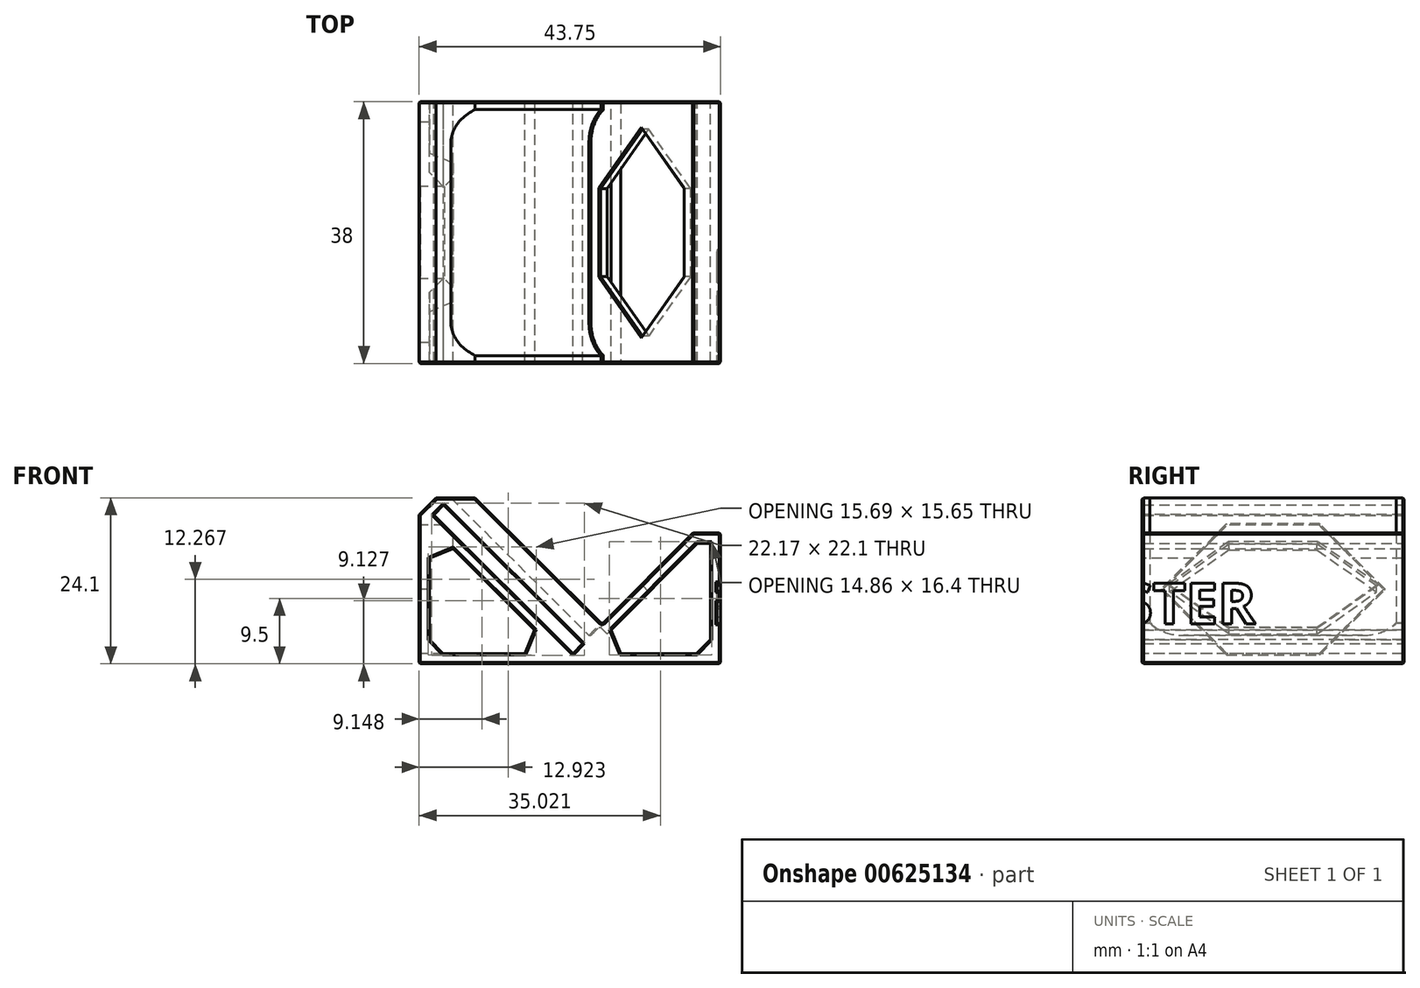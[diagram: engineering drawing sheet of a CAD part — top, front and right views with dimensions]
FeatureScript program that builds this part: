
annotation { "Feature Type Name" : "Feature", "Feature Type Description" : "" }
export const myFeature = defineFeature(function(context is Context, id is Id, definition is map)
    precondition{}
    {
        {
            var Q0;
            Q0=qCreatedBy(makeId("Front.planeOp"),FACE);
            var sketch = newSketch(context, id + "F0", { "sketchPlane" : qUnion([Q0])});
            skLineSegment(sketch, "E0", {"start": v(0, 0) * mm, "end": v(0, 19) * mm});
            skLineSegment(sketch, "E1", {"start": v(-4, 19) * mm, "end": v(-18.97, 3.98) * mm});
            skLineSegment(sketch, "E2", {"start": v(-18.97, 3.98) * mm, "end": v(-40.22, 25.16) * mm});
            skLineSegment(sketch, "E3", {"start": v(-23.56, 1.5) * mm, "end": v(-42.25, 20.12) * mm});
            skPoint(sketch, "E4", {"position": v(0, 0) * mm});
            skLineSegment(sketch, "E5", {"start": v(-40.21, 23.03) * mm, "end": v(-20.03, 2.92) * mm});
            skLineSegment(sketch, "E6", {"start": v(-20.03, 2.92) * mm, "end": v(-21.44, 1.5) * mm});
            skLineSegment(sketch, "E7", {"start": v(0, 19) * mm, "end": v(-4, 19) * mm});
            skLineSegment(sketch, "E8", {"start": v(-19.32, 1.5) * mm, "end": v(-3.38, 17.5) * mm});
            skLineSegment(sketch, "E9", {"start": v(-3.38, 17.5) * mm, "end": v(-1.5, 17.5) * mm});
            skLineSegment(sketch, "E10", {"start": v(-1.5, 17.5) * mm, "end": v(-1.5, 1.5) * mm});
            skLineSegment(sketch, "E11", {"start": v(-1.5, 1.5) * mm, "end": v(-19.32, 1.5) * mm});
            skLineSegment(sketch, "E12", {"start": v(-21.44, 1.5) * mm, "end": v(-41.63, 21.62) * mm});
            skLineSegment(sketch, "E13", {"start": v(-40.21, 23.03) * mm, "end": v(-41.63, 21.62) * mm});
            skLineSegment(sketch, "E14", {"start": v(-40.22, 25.16) * mm, "end": v(-43.75, 21.61) * mm});
            skLineSegment(sketch, "E15", {"start": v(-43.75, 21.61) * mm, "end": v(-43.75, 0) * mm});
            skLineSegment(sketch, "E16", {"start": v(-43.75, 0) * mm, "end": v(0, 0) * mm});
            skLineSegment(sketch, "E17.0", {"start": v(-42.25, 1.5) * mm, "end": v(-23.56, 1.5) * mm});
            skLineSegment(sketch, "E17.1", {"start": v(-42.25, 20.12) * mm, "end": v(-42.25, 1.5) * mm});
            skSolve(sketch);
        }
        {
            var Q0;
            {var subQ3=sQuery(id+"F0.wireOp",EDGE,"E2");Q0=makeQuery(id+"F0.imprint","IMPRINT",FACE,{"disambiguationData":[TD([[makeQuery(id+"F0.imprint","IMPRINT",EDGE,{"derivedFrom":subQ3}),1.0]])]});}
            extrude(context, id + "F1", {"entities" : qUnion([Q0]), "endBound" : BoundingType.SYMMETRIC, "depth" : 38 * mm, "offsetDistance" : 25 * mm});
        }
        {
            var Q0;
            Q0=makeQuery(id+"F1.opExtrude","SWEPT_FACE",FACE,{"disambiguationData":[OSD([sQuery(id+"F0.wireOp",EDGE,"E0")])]});
            var sketch = newSketch(context, id + "F2", { "sketchPlane" : qUnion([Q0])});
            skText(sketch, "E18", { "text": "AIRSTER", "fontName": "OpenSans-Bold.ttf"});
            skPoint(sketch, "E19", {"position": v(-17, 9.5) * mm});
            skPoint(sketch, "E20", {"position": v(-19, 9.5) * mm});
            skPoint(sketch, "E21", {"position": v(0, 19) * mm});
            const initialGuessF2  = {"E18": [-0.036, 0.00576, 1, 0, 0.00598]};
            skSetInitialGuess(sketch, initialGuessF2);
            skSolve(sketch);
        }
        {
            var Q0;
            Q0=qSketchRegion(id+"F2",true);
            extrude(context, id + "F3", {"entities" : qUnion([Q0]), "operationType" : NewBodyOperationType.REMOVE, "oppositeDirection" : true, "depth" : 0.5 * mm});
        }
        {
            var Q0;
            Q0=makeQuery(id+"F1.opExtrude","SWEPT_EDGE",EDGE,{"disambiguationData":[OSD([sQuery(id+"F0.wireOp",EDGE,"E8"),sQuery(id+"F0.wireOp",EDGE,"E11")])]});
            var Q1;
            Q1=makeQuery(id+"F1.opExtrude","SWEPT_EDGE",EDGE,{"disambiguationData":[OSD([sQuery(id+"F0.wireOp",EDGE,"E10"),sQuery(id+"F0.wireOp",EDGE,"E11")])]});
            var Q2;
            Q2=makeQuery(id+"F1.opExtrude","SWEPT_EDGE",EDGE,{"disambiguationData":[OSD([sQuery(id+"F0.wireOp",EDGE,"E17.0"),sQuery(id+"F0.wireOp",EDGE,"E17.1")])]});
            var Q3;
            Q3=makeQuery(id+"F1.opExtrude","SWEPT_EDGE",EDGE,{"disambiguationData":[OSD([sQuery(id+"F0.wireOp",EDGE,"E3"),sQuery(id+"F0.wireOp",EDGE,"E17.1")])]});
            chamfer(context, id + "F4", {"entities" : qUnion([Q0, Q1, Q2, Q3]), "width" : 2 * mm, "tangentPropagation" : true});
        }
        {
            var Q0;
            Q0=makeQuery(id+"F1.opExtrude","SWEPT_FACE",FACE,{"disambiguationData":[OSD([sQuery(id+"F0.wireOp",EDGE,"E1")])]});
            var sketch = newSketch(context, id + "F5", { "sketchPlane" : qUnion([Q0])});
            skArc(sketch, "E22", {"start": v(-19, -4.57) * mm, "mid": v(-17.24, -8.81) * mm, "end": v(-13, -10.57) * mm});
            skArc(sketch, "E23.MirrorCS", {"start": v(19, -4.57) * mm, "mid": v(17.24, -8.81) * mm, "end": v(13, -10.57) * mm});
            skLineSegment(sketch, "E24", {"start": v(-19, -8.07) * mm, "end": v(-17.87, -8.07) * mm});
            skLineSegment(sketch, "E25.MirrorCS", {"start": v(19, -8.07) * mm, "end": v(17.87, -8.07) * mm});
            skLineSegment(sketch, "E26", {"start": v(0, 8.63) * mm, "end": v(-15, 8.63) * mm});
            skLineSegment(sketch, "E27", {"start": v(-15, 8.63) * mm, "end": v(-15, -8.57) * mm});
            skLineSegment(sketch, "E28", {"start": v(-15, -8.57) * mm, "end": v(0, -8.57) * mm});
            skLineSegment(sketch, "E29.MirrorCS", {"start": v(0, 8.63) * mm, "end": v(15, 8.63) * mm});
            skLineSegment(sketch, "E30.MirrorCS", {"start": v(15, 8.63) * mm, "end": v(15, -8.57) * mm});
            skLineSegment(sketch, "E31.MirrorCS", {"start": v(15, -8.57) * mm, "end": v(0, -8.57) * mm});
            skPoint(sketch, "E32", {"position": v(-15, 0.03) * mm});
            skLineSegment(sketch, "E33", {"start": v(-15, 0.03) * mm, "end": v(-6.4, 8.63) * mm});
            skLineSegment(sketch, "E34", {"start": v(-15, 0.03) * mm, "end": v(-6.4, -8.57) * mm});
            skLineSegment(sketch, "E35.MirrorCS", {"start": v(15, 0.03) * mm, "end": v(6.4, 8.63) * mm});
            skLineSegment(sketch, "E36.MirrorCS", {"start": v(15, 0.03) * mm, "end": v(6.4, -8.57) * mm});
            skSolve(sketch);
        }
        {
            var Q0;
            {var subQ4=sQuery(id+"F5.wireOp",EDGE,"E24");Q0=makeQuery(id+"F5.imprint","IMPRINT",FACE,{"disambiguationData":[TD([[makeQuery(id+"F5.imprint","IMPRINT",EDGE,{"derivedFrom":subQ4}),-1.0]])]});}
            var Q1;
            {var subQ4=sQuery(id+"F5.wireOp",EDGE,"E25.MirrorCS");Q1=makeQuery(id+"F5.imprint","IMPRINT",FACE,{"disambiguationData":[TD([[makeQuery(id+"F5.imprint","IMPRINT",EDGE,{"derivedFrom":subQ4}),1.0]])]});}
            var Q2;
            Q2=makeQuery(id+"F1.opExtrude","SWEPT_FACE",FACE,{"disambiguationData":[OSD([sQuery(id+"F0.wireOp",EDGE,"E14")])]});
            extrude(context, id + "F6", {"entities" : qUnion([Q0, Q1]), "operationType" : NewBodyOperationType.ADD, "endBound" : BoundingType.UP_TO_SURFACE, "depth" : 25 * mm, "endBoundEntityFace" : qUnion([Q2]), "offsetDistance" : 25 * mm});
        }
        {
            var Q0;
            Q0=makeQuery(id+"F6.opExtrude","CAP_EDGE",EDGE,{"disambiguationData":[OSD([sQuery(id+"F5.wireOp",EDGE,"E24")])],"isStart":false});
            var Q1;
            Q1=makeQuery(id+"F6.opExtrude","CAP_EDGE",EDGE,{"disambiguationData":[OSD([sQuery(id+"F5.wireOp",EDGE,"E25.MirrorCS")])],"isStart":false});
            chamfer(context, id + "F7", {"entities" : qUnion([Q0, Q1]), "width" : 4 * mm, "tangentPropagation" : true});
        }
        {
            var Q0;
            {var subQ7=sQuery(id+"F5.wireOp",EDGE,"E33");Q0=makeQuery(id+"F5.imprint","IMPRINT",FACE,{"disambiguationData":[TD([[makeQuery(id+"F5.imprint","IMPRINT",EDGE,{"derivedFrom":subQ7}),-1.0]])]});}
            var Q1;
            Q1=makeQuery(id+"F1.opExtrude","SWEPT_FACE",FACE,{"disambiguationData":[OSD([sQuery(id+"F0.wireOp",EDGE,"E8")])]});
            extrude(context, id + "F8", {"entities" : qUnion([Q0]), "operationType" : NewBodyOperationType.REMOVE, "endBound" : BoundingType.UP_TO_SURFACE, "oppositeDirection" : true, "depth" : 25 * mm, "endBoundEntityFace" : qUnion([Q1]), "offsetDistance" : 25 * mm});
        }
        {
            var Q0;
            Q0=makeQuery(id+"F1.opExtrude","SWEPT_FACE",FACE,{"disambiguationData":[OSD([sQuery(id+"F0.wireOp",EDGE,"E15")])]});
            var sketch = newSketch(context, id + "F9", { "sketchPlane" : qUnion([Q0])});
            skLineSegment(sketch, "E37", {"start": v(0, 20.11) * mm, "end": v(-16, 20.11) * mm});
            skLineSegment(sketch, "E38", {"start": v(-16, 20.11) * mm, "end": v(-16, 1.5) * mm});
            skLineSegment(sketch, "E39", {"start": v(-16, 1.5) * mm, "end": v(0, 1.5) * mm});
            skPoint(sketch, "E40", {"position": v(-16, 10.8) * mm});
            skLineSegment(sketch, "E41", {"start": v(-16, 10.8) * mm, "end": v(-6.7, 20.11) * mm});
            skLineSegment(sketch, "E42", {"start": v(-16, 10.8) * mm, "end": v(-6.7, 1.5) * mm});
            skLineSegment(sketch, "E43.MirrorCS", {"start": v(0, 20.11) * mm, "end": v(16, 20.11) * mm});
            skLineSegment(sketch, "E44.MirrorCS", {"start": v(16, 10.8) * mm, "end": v(6.7, 20.11) * mm});
            skLineSegment(sketch, "E45.MirrorCS", {"start": v(16, 10.8) * mm, "end": v(6.7, 1.5) * mm});
            skLineSegment(sketch, "E46.MirrorCS", {"start": v(16, 1.5) * mm, "end": v(0, 1.5) * mm});
            skLineSegment(sketch, "E47.MirrorCS", {"start": v(16, 20.11) * mm, "end": v(16, 1.5) * mm});
            skSolve(sketch);
        }
        {
            var Q0;
            {var subQ1=sQuery(id+"F9.wireOp",EDGE,"E41");Q0=makeQuery(id+"F9.imprint","IMPRINT",FACE,{"disambiguationData":[TD([[makeQuery(id+"F9.imprint","IMPRINT",EDGE,{"derivedFrom":subQ1}),-1.0]])]});}
            var Q1;
            {var subQ0=sQuery(id+"F0.wireOp",EDGE,"E3");var subQ1=sQuery(id+"F0.wireOp",EDGE,"E17.1");Q1=makeQuery(id+"F4.opChamfer","BLEND_VERTEX",VERTEX,{"blendedFrom":[makeQuery(id+"F1.opExtrude","SWEPT_EDGE",EDGE,{"disambiguationData":[OSD([subQ0,subQ1])]}),makeQuery(id+"F1.opExtrude","CAP_FACE",FACE,{"disambiguationData":[OSD([sQuery(id+"F0.wireOp",EDGE,"E0"),sQuery(id+"F0.wireOp",EDGE,"E1"),sQuery(id+"F0.wireOp",EDGE,"E2"),subQ0,sQuery(id+"F0.wireOp",EDGE,"E5"),sQuery(id+"F0.wireOp",EDGE,"E6"),sQuery(id+"F0.wireOp",EDGE,"E7"),sQuery(id+"F0.wireOp",EDGE,"E8"),sQuery(id+"F0.wireOp",EDGE,"E9"),sQuery(id+"F0.wireOp",EDGE,"E10"),sQuery(id+"F0.wireOp",EDGE,"E11"),sQuery(id+"F0.wireOp",EDGE,"E12"),sQuery(id+"F0.wireOp",EDGE,"E13"),sQuery(id+"F0.wireOp",EDGE,"E14"),sQuery(id+"F0.wireOp",EDGE,"E15"),sQuery(id+"F0.wireOp",EDGE,"E16"),sQuery(id+"F0.wireOp",EDGE,"E17.0"),subQ1])],"isStart":true}),makeQuery(id+"F1.opExtrude","SWEPT_FACE",FACE,{"disambiguationData":[OSD([subQ0])]})],"blendedInto":[makeQuery(id+"F1.opExtrude","CAP_FACE",FACE,{"disambiguationData":[OSD([sQuery(id+"F0.wireOp",EDGE,"E0"),sQuery(id+"F0.wireOp",EDGE,"E1"),sQuery(id+"F0.wireOp",EDGE,"E2"),subQ0,sQuery(id+"F0.wireOp",EDGE,"E5"),sQuery(id+"F0.wireOp",EDGE,"E6"),sQuery(id+"F0.wireOp",EDGE,"E7"),sQuery(id+"F0.wireOp",EDGE,"E8"),sQuery(id+"F0.wireOp",EDGE,"E9"),sQuery(id+"F0.wireOp",EDGE,"E10"),sQuery(id+"F0.wireOp",EDGE,"E11"),sQuery(id+"F0.wireOp",EDGE,"E12"),sQuery(id+"F0.wireOp",EDGE,"E13"),sQuery(id+"F0.wireOp",EDGE,"E14"),sQuery(id+"F0.wireOp",EDGE,"E15"),sQuery(id+"F0.wireOp",EDGE,"E16"),sQuery(id+"F0.wireOp",EDGE,"E17.0"),subQ1])],"isStart":true}),makeQuery(id+"F1.opExtrude","SWEPT_FACE",FACE,{"disambiguationData":[OSD([subQ0])]})]});}
            extrude(context, id + "F10", {"entities" : qUnion([Q0]), "operationType" : NewBodyOperationType.REMOVE, "endBound" : BoundingType.UP_TO_VERTEX, "oppositeDirection" : true, "depth" : 25 * mm, "endBoundEntityVertex" : qUnion([Q1]), "offsetDistance" : 25 * mm});
        }
        {
            var Q0;
            Q0=makeQuery(id+"F1.opExtrude","SWEPT_EDGE",EDGE,{"disambiguationData":[OSD([sQuery(id+"F0.wireOp",EDGE,"E3"),sQuery(id+"F0.wireOp",EDGE,"E17.0")])]});
            chamfer(context, id + "F11", {"entities" : qUnion([Q0]), "width" : 2 * mm, "tangentPropagation" : true});
        }
        {
            var Q0;
            {var subQ0=sQuery(id+"F0.wireOp",EDGE,"E1");var subQ1=makeQuery(id+"F1.opExtrude","CAP_EDGE",EDGE,{"disambiguationData":[OSD([subQ0])],"isStart":false});var subQ2=sQuery(id+"F0.wireOp",EDGE,"E2");Q0=makeQuery(id+"F6.boolean.opBoolean","MERGE",FACE,{"derivedFrom":[makeQuery(id+"F1.opExtrude","CAP_FACE",FACE,{"disambiguationData":[OSD([sQuery(id+"F0.wireOp",EDGE,"E0"),subQ0,subQ2,sQuery(id+"F0.wireOp",EDGE,"E3"),sQuery(id+"F0.wireOp",EDGE,"E5"),sQuery(id+"F0.wireOp",EDGE,"E6"),sQuery(id+"F0.wireOp",EDGE,"E7"),sQuery(id+"F0.wireOp",EDGE,"E8"),sQuery(id+"F0.wireOp",EDGE,"E9"),sQuery(id+"F0.wireOp",EDGE,"E10"),sQuery(id+"F0.wireOp",EDGE,"E11"),sQuery(id+"F0.wireOp",EDGE,"E12"),sQuery(id+"F0.wireOp",EDGE,"E13"),sQuery(id+"F0.wireOp",EDGE,"E14"),sQuery(id+"F0.wireOp",EDGE,"E15"),sQuery(id+"F0.wireOp",EDGE,"E16"),sQuery(id+"F0.wireOp",EDGE,"E17.0"),sQuery(id+"F0.wireOp",EDGE,"E17.1")])],"isStart":false}),makeQuery(id+"F6.opExtrude","SWEPT_FACE",FACE,{"disambiguationData":[OSD([subQ0]),TDD([makeQuery(id+"F5.imprint","IMPRINT",EDGE,{"disambiguationData":[TD([[makeQuery(id+"F5.imprint","INTERSECT",VERTEX,{"derivedFrom":[subQ1,sQuery(id+"F5.wireOp",EDGE,"E25.MirrorCS")]}),-1.0]])],"derivedFrom":subQ1})])]})]});}
            var Q1;
            {var subQ0=sQuery(id+"F0.wireOp",EDGE,"E1");var subQ1=makeQuery(id+"F1.opExtrude","CAP_EDGE",EDGE,{"disambiguationData":[OSD([subQ0])],"isStart":true});var subQ2=sQuery(id+"F0.wireOp",EDGE,"E2");Q1=makeQuery(id+"F6.boolean.opBoolean","MERGE",FACE,{"derivedFrom":[makeQuery(id+"F1.opExtrude","CAP_FACE",FACE,{"disambiguationData":[OSD([sQuery(id+"F0.wireOp",EDGE,"E0"),subQ0,subQ2,sQuery(id+"F0.wireOp",EDGE,"E3"),sQuery(id+"F0.wireOp",EDGE,"E5"),sQuery(id+"F0.wireOp",EDGE,"E6"),sQuery(id+"F0.wireOp",EDGE,"E7"),sQuery(id+"F0.wireOp",EDGE,"E8"),sQuery(id+"F0.wireOp",EDGE,"E9"),sQuery(id+"F0.wireOp",EDGE,"E10"),sQuery(id+"F0.wireOp",EDGE,"E11"),sQuery(id+"F0.wireOp",EDGE,"E12"),sQuery(id+"F0.wireOp",EDGE,"E13"),sQuery(id+"F0.wireOp",EDGE,"E14"),sQuery(id+"F0.wireOp",EDGE,"E15"),sQuery(id+"F0.wireOp",EDGE,"E16"),sQuery(id+"F0.wireOp",EDGE,"E17.0"),sQuery(id+"F0.wireOp",EDGE,"E17.1")])],"isStart":true}),makeQuery(id+"F6.opExtrude","SWEPT_FACE",FACE,{"disambiguationData":[OSD([subQ0]),TDD([makeQuery(id+"F5.imprint","IMPRINT",EDGE,{"disambiguationData":[TD([[makeQuery(id+"F5.imprint","INTERSECT",VERTEX,{"derivedFrom":[subQ1,sQuery(id+"F5.wireOp",EDGE,"E24")]}),-1.0]])],"derivedFrom":subQ1})])]})]});}
            var Q2;
            Q2=makeQuery(id+"F1.opExtrude","SWEPT_FACE",FACE,{"disambiguationData":[OSD([sQuery(id+"F0.wireOp",EDGE,"E15")])]});
            var Q3;
            Q3=makeQuery(id+"F1.opExtrude","SWEPT_EDGE",EDGE,{"disambiguationData":[OSD([sQuery(id+"F0.wireOp",EDGE,"E0"),sQuery(id+"F0.wireOp",EDGE,"E7")])]});
            var Q4;
            Q4=makeQuery(id+"F1.opExtrude","SWEPT_EDGE",EDGE,{"disambiguationData":[OSD([sQuery(id+"F0.wireOp",EDGE,"E0"),sQuery(id+"F0.wireOp",EDGE,"E16")])]});
            var Q5;
            Q5=makeQuery(id+"F1.opExtrude","SWEPT_FACE",FACE,{"disambiguationData":[OSD([sQuery(id+"F0.wireOp",EDGE,"E1")])]});
            chamfer(context, id + "F12", {"entities" : qUnion([Q0, Q1, Q2, Q3, Q4, Q5]), "width" : 0.2 * mm, "tangentPropagation" : true});
        }
    });
